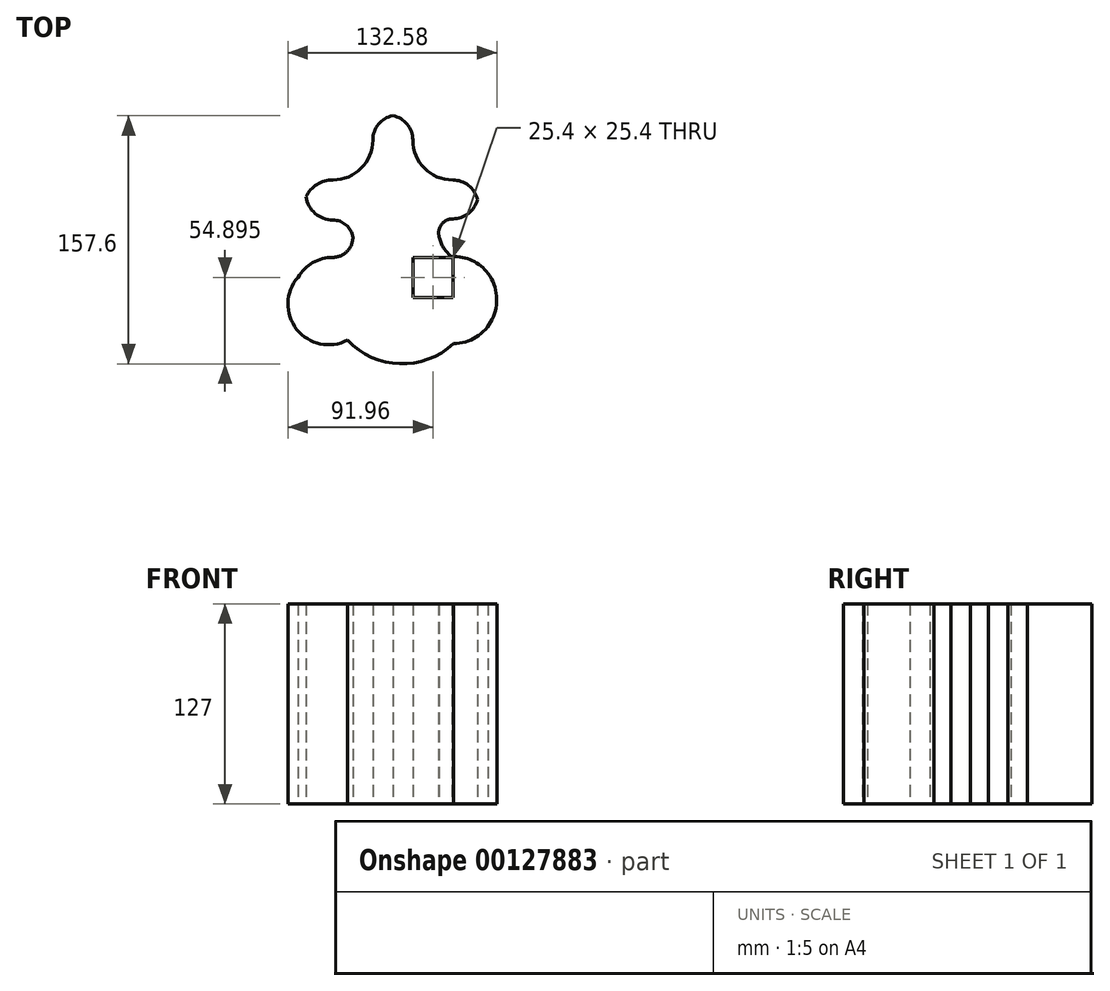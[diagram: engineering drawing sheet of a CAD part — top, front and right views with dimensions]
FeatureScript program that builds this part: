
annotation { "Feature Type Name" : "Feature", "Feature Type Description" : "" }
export const myFeature = defineFeature(function(context is Context, id is Id, definition is map)
    precondition{}
    {
        {
            var Q0;
            Q0=qCreatedBy(makeId("Top.planeOp"),FACE);
            var sketch = newSketch(context, id + "F0", { "sketchPlane" : qUnion([Q0])});
            skLineSegment(sketch, "E0", {"start": v(0, 58.44) * mm, "end": v(12.7, 58.44) * mm});
            skLineSegment(sketch, "E1", {"start": v(0, 58.44) * mm, "end": v(-12.7, 58.44) * mm});
            skLineSegment(sketch, "E2", {"start": v(-12.7, 58.44) * mm, "end": v(-12.7, 33.04) * mm});
            skLineSegment(sketch, "E3", {"start": v(12.7, 58.44) * mm, "end": v(12.7, 33.04) * mm});
            skLineSegment(sketch, "E4", {"start": v(12.7, 33.04) * mm, "end": v(12.7, 45.74) * mm});
            skLineSegment(sketch, "E5", {"start": v(12.7, 33.04) * mm, "end": v(38.1, 33.04) * mm});
            skLineSegment(sketch, "E6", {"start": v(-12.7, 33.04) * mm, "end": v(-38.1, 33.04) * mm});
            skLineSegment(sketch, "E7", {"start": v(-38.1, 33.04) * mm, "end": v(-38.1, 7.64) * mm});
            skLineSegment(sketch, "E8", {"start": v(-38.1, 7.64) * mm, "end": v(-12.7, 7.64) * mm});
            skLineSegment(sketch, "E9", {"start": v(12.7, -49.87) * mm, "end": v(12.7, 8.34) * mm});
            skLineSegment(sketch, "E10", {"start": v(12.7, 8.34) * mm, "end": v(38.1, 8.34) * mm});
            skLineSegment(sketch, "E11", {"start": v(38.1, 8.34) * mm, "end": v(38.1, 33.04) * mm});
            skLineSegment(sketch, "E12", {"start": v(-12.7, 7.64) * mm, "end": v(-12.7, -49.87) * mm});
            skLineSegment(sketch, "E13", {"start": v(-12.7, -49.87) * mm, "end": v(12.7, -49.87) * mm});
            skLineSegment(sketch, "E14", {"start": v(12.7, -16.1) * mm, "end": v(38.1, -16.1) * mm});
            skLineSegment(sketch, "E15", {"start": v(38.1, -16.1) * mm, "end": v(38.1, -41.5) * mm});
            skLineSegment(sketch, "E16", {"start": v(38.1, -41.5) * mm, "end": v(12.7, -41.5) * mm});
            skLineSegment(sketch, "E17", {"start": v(-12.7, -16.1) * mm, "end": v(-38.1, -16.1) * mm});
            skLineSegment(sketch, "E18", {"start": v(-38.1, -16.1) * mm, "end": v(-38.1, -41.5) * mm});
            skLineSegment(sketch, "E19", {"start": v(-38.1, -41.5) * mm, "end": v(-12.7, -41.5) * mm});
            skArc(sketch, "E20", {"start": v(0, 73.9) * mm, "mid": v(-9.12, 68.45) * mm, "end": v(-12.7, 58.44) * mm});
            skArc(sketch, "E21", {"start": v(12.7, 58.44) * mm, "mid": v(9.12, 68.45) * mm, "end": v(0, 73.9) * mm});
            skArc(sketch, "E22", {"start": v(12.7, 58.44) * mm, "mid": v(20.14, 40.48) * mm, "end": v(38.1, 33.04) * mm});
            skArc(sketch, "E23", {"start": v(-38.1, 33.04) * mm, "mid": v(-20.14, 40.48) * mm, "end": v(-12.7, 58.44) * mm});
            skArc(sketch, "E24", {"start": v(53.83, 20.7) * mm, "mid": v(48.1, 29.59) * mm, "end": v(38.1, 33.04) * mm});
            skPoint(sketch, "E24.startSnap0", {"position": v(38.1, 20.7) * mm});
            skArc(sketch, "E25", {"start": v(38.1, 8.34) * mm, "mid": v(48.1, 11.8) * mm, "end": v(53.83, 20.7) * mm});
            skArc(sketch, "E26", {"start": v(-38.1, 33.04) * mm, "mid": v(-48.18, 30.16) * mm, "end": v(-55.2, 22.39) * mm});
            skArc(sketch, "E27", {"start": v(-55.2, 22.39) * mm, "mid": v(-49.4, 11.84) * mm, "end": v(-38.1, 7.64) * mm});
            skArc(sketch, "E28", {"start": v(38.1, 8.34) * mm, "mid": v(30.95, 4.8) * mm, "end": v(29.42, -3.04) * mm});
            skArc(sketch, "E29", {"start": v(29.42, -3.04) * mm, "mid": v(32.43, -10.45) * mm, "end": v(38.1, -16.1) * mm});
            skArc(sketch, "E30", {"start": v(60.52, -26.45) * mm, "mid": v(50.25, -17.97) * mm, "end": v(37.1, -15.75) * mm});
            skArc(sketch, "E31", {"start": v(39.52, -41.43) * mm, "mid": v(53.08, -38.22) * mm, "end": v(60.52, -26.45) * mm});
            skArc(sketch, "E32", {"start": v(-25.4, -3.37) * mm, "mid": v(-29.7, 4.5) * mm, "end": v(-38.1, 7.64) * mm});
            skPoint(sketch, "E32.startSnap0", {"position": v(-25.4, 7.64) * mm});
            skArc(sketch, "E33", {"start": v(-38.1, -16.1) * mm, "mid": v(-29.1, -12.37) * mm, "end": v(-25.4, -3.37) * mm});
            skArc(sketch, "E34", {"start": v(-38.1, -16.1) * mm, "mid": v(-50.86, -19.5) * mm, "end": v(-60.22, -28.8) * mm});
            skPoint(sketch, "E34.endSnap0", {"position": v(-38.1, -28.8) * mm});
            skArc(sketch, "E35", {"start": v(-60.22, -28.8) * mm, "mid": v(-50.86, -38.1) * mm, "end": v(-38.1, -41.5) * mm});
            skArc(sketch, "E36", {"start": v(-38.1, -41.5) * mm, "mid": v(-28.74, -68.72) * mm, "end": v(0, -67.26) * mm});
            skArc(sketch, "E37", {"start": v(38.45, -70.94) * mm, "mid": v(63.11, -55.46) * mm, "end": v(60.52, -26.45) * mm});
            skArc(sketch, "E38", {"start": v(-60.22, -28.8) * mm, "mid": v(-61, -61.79) * mm, "end": v(-28.74, -68.72) * mm});
            skArc(sketch, "E39", {"start": v(-28.74, -68.72) * mm, "mid": v(4.4, -83.68) * mm, "end": v(38.45, -70.94) * mm});
            skSolve(sketch);
        }
        {
            var Q0;
            Q0=qSketchRegion(id+"F0",true);
            extrude(context, id + "F1", {"entities" : qUnion([Q0]), "endBound" : BoundingType.SYMMETRIC, "depth" : 127 * mm});
        }
    });
